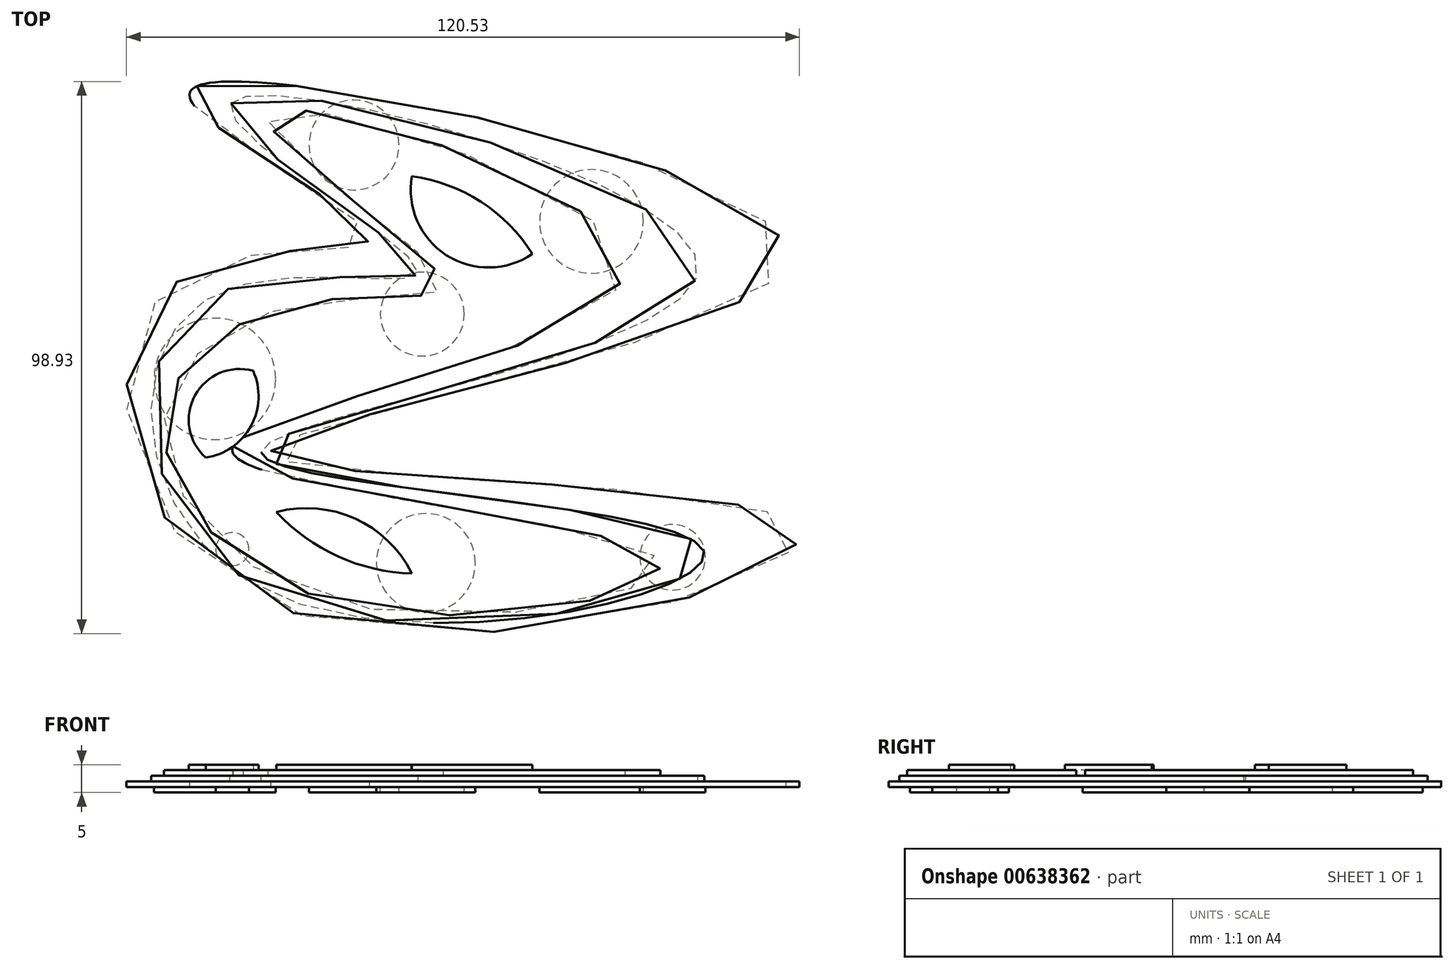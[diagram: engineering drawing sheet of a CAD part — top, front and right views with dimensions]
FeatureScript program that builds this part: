
annotation { "Feature Type Name" : "Feature", "Feature Type Description" : "" }
export const myFeature = defineFeature(function(context is Context, id is Id, definition is map)
    precondition{}
    {
        {
            var Q0;
            Q0=qCreatedBy(makeId("Top.planeOp"),FACE);
            var sketch = newSketch(context, id + "F0", { "sketchPlane" : qUnion([Q0])});
            skFitSpline(sketch, "E0", {"points": [v(-58.83, 32.79) * mm, v(28.12, 0) * mm, v(-63.4, -33) * mm, v(30.6, -46.07) * mm, v(-64.43, -59.76) * mm, v(-80.83, -2.7) * mm, v(-45.76, 5.6) * mm, v(-77.3, 29.47) * mm, v(-58.83, 32.79) * mm]});
            skSolve(sketch);
        }
        {
            var Q0;
            Q0 = qSketchRegion(id + "F0", true);
            var Q1;
            Q1 = qSketchRegion(id + "F4", true);
            extrude(context, id + "F1", {"entities" : qUnion([Q0, Q1]), "depth" : 1 * mm, "offsetDistance" : 25 * mm});
        }
        {
            var Q0;
            Q0=qCreatedBy(makeId("Top.planeOp"),FACE);
            var sketch = newSketch(context, id + "F2", { "sketchPlane" : qUnion([Q0])});
            skFitSpline(sketch, "E1", {"points": [v(-70.53, 29.67) * mm, v(13.1, 0) * mm, v(-65.13, -32.79) * mm, v(13.72, -49.8) * mm, v(-65.55, -57.07) * mm, v(-74.88, -5.4) * mm, v(-37.12, 0) * mm, v(-70.53, 29.67) * mm]});
            skSolve(sketch);
        }
        {
            var Q0;
            Q0 = qSketchRegion(id + "F2", true);
            var Q1;
            Q1 = qSketchRegion(id + "F4", true);
            extrude(context, id + "F3", {"entities" : qUnion([Q0, Q1]), "operationType" : NewBodyOperationType.ADD, "depth" : 2 * mm, "offsetDistance" : 25 * mm});
        }
        {
            var Q0;
            Q0=qCreatedBy(makeId("Top.planeOp"),FACE);
            var sketch = newSketch(context, id + "F4", { "sketchPlane" : qUnion([Q0])});
            skFitSpline(sketch, "E2", {"points": [v(-63.68, 27.6) * mm, v(0, 0) * mm, v(-70.32, -32.37) * mm, v(5.63, -51.67) * mm, v(-49.98, -60.18) * mm, v(-82.35, -26.15) * mm, v(-55.59, -5.81) * mm, v(-32.76, -1.87) * mm, v(-63.68, 27.6) * mm]});
            skSolve(sketch);
        }
        {
            var Q0;
            Q0 = qSketchRegion(id + "F4", true);
            extrude(context, id + "F5", {"entities" : qUnion([Q0]), "operationType" : NewBodyOperationType.ADD, "depth" : 3 * mm, "offsetDistance" : 25 * mm});
        }
        {
            var Q0;
            Q0=qCreatedBy(makeId("Top.planeOp"),FACE);
            var sketch = newSketch(context, id + "F6", { "sketchPlane" : qUnion([Q0])});
            skArc(sketch, "E3", {"start": v(-38.14, 16.6) * mm, "mid": v(-31.97, 2.48) * mm, "end": v(-16.56, 2.7) * mm});
            skArc(sketch, "E4", {"start": v(-16.56, 2.7) * mm, "mid": v(-25.8, 12.05) * mm, "end": v(-38.14, 16.6) * mm});
            skArc(sketch, "E5", {"start": v(-66.57, -18.26) * mm, "mid": v(-76.99, -22.67) * mm, "end": v(-75.08, -33.82) * mm});
            skArc(sketch, "E6", {"start": v(-75.08, -33.82) * mm, "mid": v(-66.96, -28.15) * mm, "end": v(-66.57, -18.26) * mm});
            skArc(sketch, "E7", {"start": v(-38.14, -54.58) * mm, "mid": v(-48.32, -44.74) * mm, "end": v(-62.42, -43.58) * mm});
            skArc(sketch, "E8", {"start": v(-62.42, -43.58) * mm, "mid": v(-51.38, -51.52) * mm, "end": v(-38.14, -54.58) * mm});
            skSolve(sketch);
        }
        {
            var Q0;
            Q0 = qSketchRegion(id + "F6", true);
            extrude(context, id + "F7", {"entities" : qUnion([Q0]), "operationType" : NewBodyOperationType.ADD, "depth" : 4 * mm, "offsetDistance" : 25 * mm});
        }
        {
            var Q0;
            Q0=qCreatedBy(makeId("Top.planeOp"),FACE);
            var sketch = newSketch(context, id + "F8", { "sketchPlane" : qUnion([Q0])});
            skCircle(sketch, "E9", {"center": v(-36.27, -8.1) * mm, "radius": 7.52 * mm});
            skCircle(sketch, "E10", {"center": v(-35.65, -52.7) * mm, "radius": 8.86 * mm});
            skCircle(sketch, "E11", {"center": v(-73.42, -19.71) * mm, "radius": 10.88 * mm});
            skCircle(sketch, "E12", {"center": v(-5.98, 8.5) * mm, "radius": 9.3 * mm});
            skCircle(sketch, "E13", {"center": v(-48.51, 22.2) * mm, "radius": 8.06 * mm});
            skCircle(sketch, "E14", {"center": v(8.55, -51.67) * mm, "radius": 5.87 * mm});
            skCircle(sketch, "E15", {"center": v(-70.3, -50.22) * mm, "radius": 2.97 * mm});
            skSolve(sketch);
        }
        {
            var Q0;
            Q0 = qSketchRegion(id + "F8", true);
            extrude(context, id + "F9", {"entities" : qUnion([Q0]), "operationType" : NewBodyOperationType.ADD, "oppositeDirection" : true, "depth" : 1 * mm, "offsetDistance" : 25 * mm});
        }
    });
